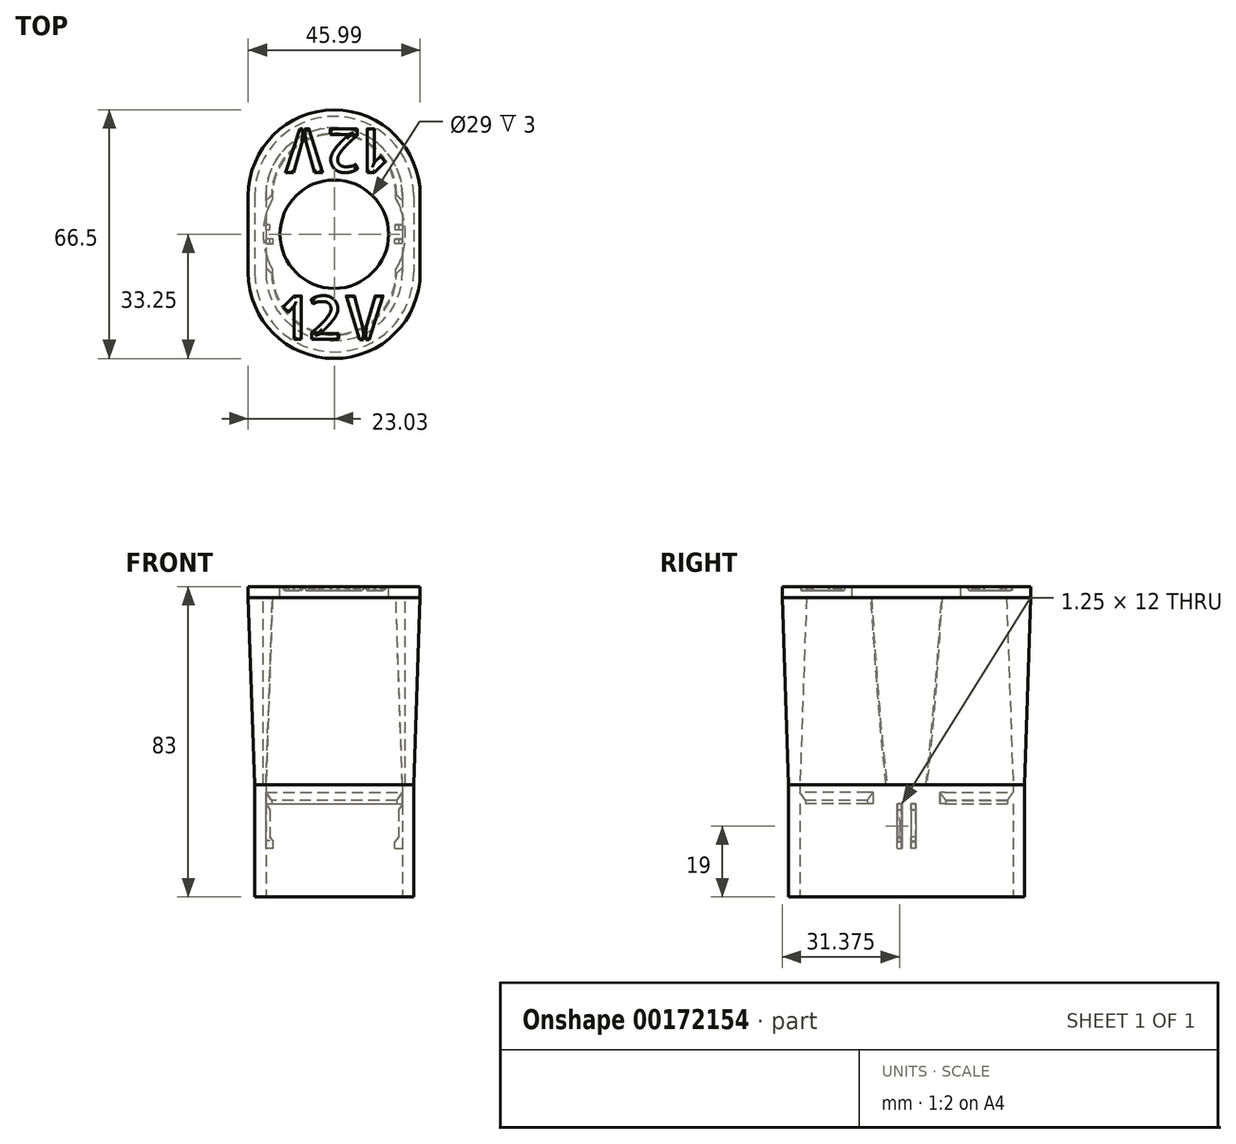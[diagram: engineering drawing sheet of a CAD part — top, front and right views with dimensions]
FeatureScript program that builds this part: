
annotation { "Feature Type Name" : "Feature", "Feature Type Description" : "" }
export const myFeature = defineFeature(function(context is Context, id is Id, definition is map)
    precondition{}
    {
        {
            var Q0;
            Q0=qCreatedBy(makeId("Top.planeOp"),FACE);
            var sketch = newSketch(context, id + "F0", { "sketchPlane" : qUnion([Q0])});
            skLineSegment(sketch, "E0", {"start": v(-18.28, 10.25) * mm, "end": v(-18.28, -10.25) * mm});
            skLineSegment(sketch, "E1", {"start": v(18.22, 10.25) * mm, "end": v(18.22, -10.25) * mm});
            skArc(sketch, "E2", {"start": v(18.22, 10.25) * mm, "mid": v(-0.03, 28.5) * mm, "end": v(-18.28, 10.25) * mm});
            skArc(sketch, "E3", {"start": v(-18.28, -10.25) * mm, "mid": v(-0.03, -28.5) * mm, "end": v(18.22, -10.25) * mm});
            skPoint(sketch, "E4", {"position": v(-0.03, 28.5) * mm});
            skPoint(sketch, "E5", {"position": v(-0.03, -28.5) * mm});
            skLineSegment(sketch, "E6.0", {"start": v(21.22, 10.25) * mm, "end": v(21.22, -10.25) * mm});
            skArc(sketch, "E6.1", {"start": v(21.22, 10.25) * mm, "mid": v(-0.03, 31.5) * mm, "end": v(-21.28, 10.25) * mm});
            skLineSegment(sketch, "E6.2", {"start": v(-21.28, 10.25) * mm, "end": v(-21.28, -10.25) * mm});
            skArc(sketch, "E6.3", {"start": v(-21.28, -10.25) * mm, "mid": v(-0.03, -31.5) * mm, "end": v(21.22, -10.25) * mm});
            skPoint(sketch, "E7", {"position": v(-18.28, 0) * mm});
            skSolve(sketch);
        }
        {
            var Q0;
            Q0=makeQuery(id+"F0.imprint","IMPRINT",FACE,{"disambiguationData":[TD([[makeQuery(id+"F0.imprint","IMPRINT",EDGE,{"derivedFrom":sQuery(id+"F0.wireOp",EDGE,"E0")}),-1.0]])]});
            extrude(context, id + "F1", {"entities" : qUnion([Q0]), "depth" : 50 * mm, "hasDraft" : true, "draftAngle" : 2 * degree, "hasSecondDirection" : true, "secondDirectionOppositeDirection" : true, "secondDirectionDepth" : 30 * mm});
        }
        {
            var Q0;
            Q0=makeQuery(id+"F1.opExtrude","CAP_FACE",FACE,{"disambiguationData":[OSD([sQuery(id+"F0.wireOp",EDGE,"E0"),sQuery(id+"F0.wireOp",EDGE,"E1"),sQuery(id+"F0.wireOp",EDGE,"E2"),sQuery(id+"F0.wireOp",EDGE,"E3"),sQuery(id+"F0.wireOp",EDGE,"E6.0"),sQuery(id+"F0.wireOp",EDGE,"E6.1"),sQuery(id+"F0.wireOp",EDGE,"E6.2"),sQuery(id+"F0.wireOp",EDGE,"E6.3")])],"isStart":false});
            var sketch = newSketch(context, id + "F2", { "sketchPlane" : qUnion([Q0])});
            skCircle(sketch, "E8", {"center": v(0, 0) * mm, "radius": 19 * mm});
            skSolve(sketch);
        }
        {
            var Q0;
            Q0 = qSketchRegion(id + "F2", true);
            extrude(context, id + "F3", {"entities" : qUnion([Q0]), "operationType" : NewBodyOperationType.REMOVE, "endBound" : BoundingType.SYMMETRIC, "oppositeDirection" : true, "depth" : 100 * mm});
        }
        {
            var Q0;
            Q0=makeQuery(id+"F1.opExtrude","CAP_FACE",FACE,{"disambiguationData":[OSD([sQuery(id+"F0.wireOp",EDGE,"E0"),sQuery(id+"F0.wireOp",EDGE,"E1"),sQuery(id+"F0.wireOp",EDGE,"E2"),sQuery(id+"F0.wireOp",EDGE,"E3"),sQuery(id+"F0.wireOp",EDGE,"E6.0"),sQuery(id+"F0.wireOp",EDGE,"E6.1"),sQuery(id+"F0.wireOp",EDGE,"E6.2"),sQuery(id+"F0.wireOp",EDGE,"E6.3")])],"isStart":false});
            var sketch = newSketch(context, id + "F4", { "sketchPlane" : qUnion([Q0])});
            skLineSegment(sketch, "E9", {"start": v(22.96, 10.25) * mm, "end": v(22.96, -10.25) * mm});
            skLineSegment(sketch, "E10", {"start": v(-23.03, 10.25) * mm, "end": v(-23.03, -10.25) * mm});
            skArc(sketch, "E11", {"start": v(22.96, 10.25) * mm, "mid": v(-0.03, 33.25) * mm, "end": v(-23.03, 10.25) * mm});
            skArc(sketch, "E12", {"start": v(-23.03, -10.25) * mm, "mid": v(-0.03, -33.25) * mm, "end": v(22.96, -10.25) * mm});
            skSolve(sketch);
        }
        {
            var Q0;
            Q0 = qSketchRegion(id + "F4", true);
            extrude(context, id + "F5", {"entities" : qUnion([Q0]), "operationType" : NewBodyOperationType.ADD, "depth" : 3 * mm});
        }
        {
            var Q0;
            Q0=makeQuery(id+"F5.opExtrude","CAP_FACE",FACE,{"disambiguationData":[OSD([sQuery(id+"F4.wireOp",EDGE,"E9"),sQuery(id+"F4.wireOp",EDGE,"E10"),sQuery(id+"F4.wireOp",EDGE,"E11"),sQuery(id+"F4.wireOp",EDGE,"E12")])],"isStart":false});
            var sketch = newSketch(context, id + "F6", { "sketchPlane" : qUnion([Q0])});
            skCircle(sketch, "E13", {"center": v(0, 0) * mm, "radius": 14.5 * mm});
            skSolve(sketch);
        }
        {
            var Q0;
            Q0 = qSketchRegion(id + "F6", true);
            extrude(context, id + "F7", {"entities" : qUnion([Q0]), "operationType" : NewBodyOperationType.REMOVE, "oppositeDirection" : true, "depth" : 25 * mm});
        }
        {
            var Q0;
            Q0=makeQuery(id+"F1.opExtrude","CAP_FACE",FACE,{"disambiguationData":[OSD([sQuery(id+"F0.wireOp",EDGE,"E0"),sQuery(id+"F0.wireOp",EDGE,"E1"),sQuery(id+"F0.wireOp",EDGE,"E2"),sQuery(id+"F0.wireOp",EDGE,"E3"),sQuery(id+"F0.wireOp",EDGE,"E6.0"),sQuery(id+"F0.wireOp",EDGE,"E6.1"),sQuery(id+"F0.wireOp",EDGE,"E6.2"),sQuery(id+"F0.wireOp",EDGE,"E6.3")])],"isStart":true});
            var sketch = newSketch(context, id + "F8", { "sketchPlane" : qUnion([Q0])});
            skLineSegment(sketch, "E14", {"start": v(-18.28, -10.25) * mm, "end": v(-18.28, -3.5) * mm});
            skLineSegment(sketch, "E15", {"start": v(18.22, -10.25) * mm, "end": v(18.22, -3.5) * mm});
            skArc(sketch, "E16", {"start": v(-18.28, -10.25) * mm, "mid": v(-0.03, -28.5) * mm, "end": v(18.22, -10.25) * mm});
            skArc(sketch, "E17", {"start": v(18.22, 10.25) * mm, "mid": v(-0.03, 28.5) * mm, "end": v(-18.28, 10.25) * mm});
            skLineSegment(sketch, "E18.0", {"start": v(-16.78, -10.25) * mm, "end": v(-16.78, -3.5) * mm});
            skArc(sketch, "E18.1", {"start": v(-16.78, -10.25) * mm, "mid": v(-0.03, -27) * mm, "end": v(16.72, -10.25) * mm});
            skLineSegment(sketch, "E18.2", {"start": v(16.72, -10.25) * mm, "end": v(16.72, -3.5) * mm});
            skArc(sketch, "E18.3", {"start": v(16.72, 10.25) * mm, "mid": v(-0.03, 27) * mm, "end": v(-16.78, 10.25) * mm});
            skPoint(sketch, "E19", {"position": v(-16.78, 0) * mm});
            skPoint(sketch, "E20", {"position": v(16.72, 0) * mm});
            skLineSegment(sketch, "E21.bottom", {"start": v(18.22, 3.5) * mm, "end": v(16.72, 3.5) * mm});
            skLineSegment(sketch, "E21.top", {"start": v(18.22, -3.5) * mm, "end": v(16.72, -3.5) * mm});
            skLineSegment(sketch, "E22.bottom", {"start": v(-18.28, 3.5) * mm, "end": v(-16.78, 3.5) * mm});
            skLineSegment(sketch, "E22.top", {"start": v(-18.28, -3.5) * mm, "end": v(-16.78, -3.5) * mm});
            skLineSegment(sketch, "E23.trimOffspring", {"start": v(-16.78, 3.5) * mm, "end": v(-16.78, 10.25) * mm});
            skPoint(sketch, "E22.right.end.orphan", {"position": v(-15.28, -3.5) * mm});
            skPoint(sketch, "E22.right.start.orphan", {"position": v(-15.28, 3.5) * mm});
            skLineSegment(sketch, "E24.trimOffspring", {"start": v(-18.28, 3.5) * mm, "end": v(-18.28, 10.25) * mm});
            skPoint(sketch, "E25.orphan", {"position": v(15.22, -3.5) * mm});
            skPoint(sketch, "E26.orphan", {"position": v(15.22, 3.5) * mm});
            skLineSegment(sketch, "E27.trimOffspring", {"start": v(16.72, 3.5) * mm, "end": v(16.72, 10.25) * mm});
            skLineSegment(sketch, "E28.trimOffspring", {"start": v(18.22, 3.5) * mm, "end": v(18.22, 10.25) * mm});
            skSolve(sketch);
        }
        {
            var Q0;
            Q0=makeQuery(id+"F8.imprint","IMPRINT",FACE,{"disambiguationData":[TD([[makeQuery(id+"F8.imprint","IMPRINT",EDGE,{"derivedFrom":sQuery(id+"F8.wireOp",EDGE,"E17")}),-1.0]])]});
            var Q1;
            Q1=makeQuery(id+"F8.imprint","IMPRINT",FACE,{"disambiguationData":[TD([[makeQuery(id+"F8.imprint","IMPRINT",EDGE,{"derivedFrom":sQuery(id+"F8.wireOp",EDGE,"E14")}),-1.0]])]});
            extrude(context, id + "F9", {"entities" : qUnion([Q0, Q1]), "operationType" : NewBodyOperationType.ADD, "oppositeDirection" : true, "depth" : 28 * mm, "hasSecondDirection" : true, "secondDirectionOppositeDirection" : true, "secondDirectionDepth" : 25 * mm});
        }
        {
            var Q0;
            Q0=makeQuery(id+"F9.opExtrude","SWEPT_EDGE",EDGE,{"disambiguationData":[OSD([sQuery(id+"F8.wireOp",EDGE,"E21.bottom"),sQuery(id+"F8.wireOp",EDGE,"E27.trimOffspring")])]});
            var Q1;
            Q1=makeQuery(id+"F9.opExtrude","SWEPT_EDGE",EDGE,{"disambiguationData":[OSD([sQuery(id+"F8.wireOp",EDGE,"E18.2"),sQuery(id+"F8.wireOp",EDGE,"E21.top")])]});
            var Q2;
            Q2=makeQuery(id+"F9.opExtrude","SWEPT_EDGE",EDGE,{"disambiguationData":[OSD([sQuery(id+"F8.wireOp",EDGE,"E22.bottom"),sQuery(id+"F8.wireOp",EDGE,"E23.trimOffspring")])]});
            var Q3;
            Q3=makeQuery(id+"F9.opExtrude","SWEPT_EDGE",EDGE,{"disambiguationData":[OSD([sQuery(id+"F8.wireOp",EDGE,"E18.0"),sQuery(id+"F8.wireOp",EDGE,"E22.top")])]});
            chamfer(context, id + "F10", {"entities" : qUnion([Q0, Q1, Q2, Q3]), "width" : 7 * mm, "tangentPropagation" : true});
        }
        {
            var Q0;
            Q0=makeQuery(id+"F9.opExtrude","CAP_EDGE",EDGE,{"disambiguationData":[OSD([sQuery(id+"F8.wireOp",EDGE,"E18.1")])],"isStart":false});
            var Q1;
            Q1=makeQuery(id+"F9.opExtrude","CAP_EDGE",EDGE,{"disambiguationData":[OSD([sQuery(id+"F8.wireOp",EDGE,"E18.3")])],"isStart":false});
            chamfer(context, id + "F11", {"entities" : qUnion([Q0, Q1]), "chamferType" : ChamferType.OFFSET_ANGLE, "width" : 1.5 * mm, "oppositeDirection" : false, "angle" : 55 * degree, "tangentPropagation" : true});
        }
        {
            var Q0;
            Q0=makeQuery(id+"F1.*.split.splitOp","SPLIT",FACE,{"derivedFrom":makeQuery(id+"F1.opExtrude","SWEPT_FACE",FACE,{"disambiguationData":[OSD([sQuery(id+"F0.wireOp",EDGE,"E1")])]}),"isFromBackBody":true});
            var sketch = newSketch(context, id + "F12", { "sketchPlane" : qUnion([Q0])});
            skLineSegment(sketch, "E29.top", {"start": v(-2.5, -5) * mm, "end": v(-1.25, -5) * mm});
            skPoint(sketch, "E30", {"position": v(0, -5) * mm});
            skLineSegment(sketch, "E31.bottom", {"start": v(2.5, -17) * mm, "end": v(1.25, -17) * mm});
            skLineSegment(sketch, "E31.left", {"start": v(2.5, -17) * mm, "end": v(2.5, -15) * mm});
            skLineSegment(sketch, "E31.right", {"start": v(-2.5, -17) * mm, "end": v(-2.5, -15) * mm});
            skLineSegment(sketch, "E32.bottom", {"start": v(-2.5, -17) * mm, "end": v(-1.25, -17) * mm});
            skLineSegment(sketch, "E32.top", {"start": v(-2.5, -15) * mm, "end": v(-1.25, -15) * mm});
            skLineSegment(sketch, "E33.left", {"start": v(1.25, -17) * mm, "end": v(1.25, -15) * mm});
            skLineSegment(sketch, "E33.right", {"start": v(-1.25, -17) * mm, "end": v(-1.25, -15) * mm});
            skLineSegment(sketch, "E34.trimOffspring", {"start": v(1.25, -15) * mm, "end": v(2.5, -15) * mm});
            skLineSegment(sketch, "E35.trimOffspring", {"start": v(1.25, -17) * mm, "end": v(2.5, -17) * mm});
            skLineSegment(sketch, "E36.trimOffspring", {"start": v(-1.25, -17) * mm, "end": v(-2.5, -17) * mm});
            skLineSegment(sketch, "E37.trimOffspring", {"start": v(1.25, -5) * mm, "end": v(2.5, -5) * mm});
            skLineSegment(sketch, "E38", {"start": v(-2.5, -5) * mm, "end": v(-2.5, -15) * mm});
            skLineSegment(sketch, "E39", {"start": v(-1.25, -5) * mm, "end": v(-1.25, -15) * mm});
            skLineSegment(sketch, "E40", {"start": v(1.25, -5) * mm, "end": v(1.25, -15) * mm});
            skLineSegment(sketch, "E41", {"start": v(2.5, -15) * mm, "end": v(2.5, -5) * mm});
            skSolve(sketch);
        }
        {
            var Q0;
            Q0=makeQuery(id+"F12.imprint","IMPRINT",FACE,{"disambiguationData":[TD([[makeQuery(id+"F12.imprint","IMPRINT",EDGE,{"derivedFrom":sQuery(id+"F12.wireOp",EDGE,"E34.trimOffspring")}),1.0]])]});
            var Q1;
            Q1=makeQuery(id+"F12.imprint","IMPRINT",FACE,{"disambiguationData":[TD([[makeQuery(id+"F12.imprint","IMPRINT",EDGE,{"derivedFrom":sQuery(id+"F12.wireOp",EDGE,"E29.top")}),-1.0]])]});
            extrude(context, id + "F13", {"entities" : qUnion([Q0, Q1]), "operationType" : NewBodyOperationType.ADD, "depth" : 1 * mm});
        }
        {
            var Q0;
            Q0=makeQuery(id+"F12.imprint","IMPRINT",FACE,{"disambiguationData":[TD([[makeQuery(id+"F12.imprint","IMPRINT",EDGE,{"derivedFrom":sQuery(id+"F12.wireOp",EDGE,"E31.left")}),1.0]])]});
            var Q1;
            Q1=makeQuery(id+"F12.imprint","IMPRINT",FACE,{"disambiguationData":[TD([[makeQuery(id+"F12.imprint","IMPRINT",EDGE,{"derivedFrom":sQuery(id+"F12.wireOp",EDGE,"E32.top")}),-1.0]])]});
            extrude(context, id + "F14", {"entities" : qUnion([Q0, Q1]), "operationType" : NewBodyOperationType.ADD, "depth" : 2 * mm});
        }
        {
            var Q0;
            Q0=makeQuery(id+"F1.*.split.splitOp","SPLIT",FACE,{"derivedFrom":makeQuery(id+"F1.opExtrude","SWEPT_FACE",FACE,{"disambiguationData":[OSD([sQuery(id+"F0.wireOp",EDGE,"E0")])]}),"isFromBackBody":true});
            var sketch = newSketch(context, id + "F15", { "sketchPlane" : qUnion([Q0])});
            skLineSegment(sketch, "E42.top", {"start": v(-2.52, -5) * mm, "end": v(-1.27, -5) * mm});
            skLineSegment(sketch, "E43.bottom", {"start": v(2.48, -17) * mm, "end": v(1.23, -17) * mm});
            skLineSegment(sketch, "E43.left", {"start": v(2.48, -17) * mm, "end": v(2.48, -15) * mm});
            skLineSegment(sketch, "E43.right", {"start": v(-2.52, -17) * mm, "end": v(-2.52, -15) * mm});
            skLineSegment(sketch, "E44.bottom", {"start": v(-2.52, -17) * mm, "end": v(-1.27, -17) * mm});
            skLineSegment(sketch, "E44.top", {"start": v(-2.52, -15) * mm, "end": v(-1.27, -15) * mm});
            skLineSegment(sketch, "E45.left", {"start": v(1.23, -17) * mm, "end": v(1.23, -15) * mm});
            skLineSegment(sketch, "E45.right", {"start": v(-1.27, -17) * mm, "end": v(-1.27, -15) * mm});
            skLineSegment(sketch, "E46.trimOffspring", {"start": v(1.23, -15) * mm, "end": v(2.48, -15) * mm});
            skLineSegment(sketch, "E47.trimOffspring", {"start": v(1.23, -17) * mm, "end": v(2.48, -17) * mm});
            skLineSegment(sketch, "E48.trimOffspring", {"start": v(-1.27, -17) * mm, "end": v(-2.52, -17) * mm});
            skLineSegment(sketch, "E49.trimOffspring", {"start": v(1.23, -5) * mm, "end": v(2.48, -5) * mm});
            skLineSegment(sketch, "E50", {"start": v(-2.52, -5) * mm, "end": v(-2.52, -15) * mm});
            skLineSegment(sketch, "E51", {"start": v(-1.27, -5) * mm, "end": v(-1.27, -15) * mm});
            skLineSegment(sketch, "E52", {"start": v(1.23, -5) * mm, "end": v(1.23, -15) * mm});
            skLineSegment(sketch, "E53", {"start": v(2.48, -15) * mm, "end": v(2.48, -5) * mm});
            skSolve(sketch);
        }
        {
            var Q0;
            Q0=makeQuery(id+"F15.imprint","IMPRINT",FACE,{"disambiguationData":[TD([[makeQuery(id+"F15.imprint","IMPRINT",EDGE,{"derivedFrom":sQuery(id+"F15.wireOp",EDGE,"E44.top")}),-1.0]])]});
            var Q1;
            Q1=makeQuery(id+"F15.imprint","IMPRINT",FACE,{"disambiguationData":[TD([[makeQuery(id+"F15.imprint","IMPRINT",EDGE,{"derivedFrom":sQuery(id+"F15.wireOp",EDGE,"E43.left")}),1.0]])]});
            extrude(context, id + "F16", {"entities" : qUnion([Q0, Q1]), "operationType" : NewBodyOperationType.ADD, "depth" : 2 * mm});
        }
        {
            var Q0;
            Q0=makeQuery(id+"F15.imprint","IMPRINT",FACE,{"disambiguationData":[TD([[makeQuery(id+"F15.imprint","IMPRINT",EDGE,{"derivedFrom":sQuery(id+"F15.wireOp",EDGE,"E46.trimOffspring")}),1.0]])]});
            var Q1;
            Q1=makeQuery(id+"F15.imprint","IMPRINT",FACE,{"disambiguationData":[TD([[makeQuery(id+"F15.imprint","IMPRINT",EDGE,{"derivedFrom":sQuery(id+"F15.wireOp",EDGE,"E42.top")}),-1.0]])]});
            extrude(context, id + "F17", {"entities" : qUnion([Q0, Q1]), "operationType" : NewBodyOperationType.ADD, "depth" : 1 * mm});
        }
        {
            var Q0;
            Q0=makeQuery(id+"F17.opExtrude","CAP_EDGE",EDGE,{"disambiguationData":[OSD([sQuery(id+"F15.wireOp",EDGE,"E49.trimOffspring")])],"isStart":false});
            var Q1;
            Q1=makeQuery(id+"F17.opExtrude","CAP_EDGE",EDGE,{"disambiguationData":[OSD([sQuery(id+"F15.wireOp",EDGE,"E42.top")])],"isStart":false});
            var Q2;
            Q2=makeQuery(id+"F13.opExtrude","CAP_EDGE",EDGE,{"disambiguationData":[OSD([sQuery(id+"F12.wireOp",EDGE,"E29.top")])],"isStart":false});
            var Q3;
            Q3=makeQuery(id+"F13.opExtrude","CAP_EDGE",EDGE,{"disambiguationData":[OSD([sQuery(id+"F12.wireOp",EDGE,"E37.trimOffspring")])],"isStart":false});
            chamfer(context, id + "F18", {"entities" : qUnion([Q0, Q1, Q2, Q3]), "chamferType" : ChamferType.OFFSET_ANGLE, "width" : 1 * mm, "oppositeDirection" : false, "angle" : 60 * degree, "tangentPropagation" : true});
        }
        {
            var Q0;
            Q0=makeQuery(id+"F14.opExtrude","SWEPT_FACE",FACE,{"disambiguationData":[OSD([sQuery(id+"F12.wireOp",EDGE,"E34.trimOffspring")])]});
            var Q1;
            Q1=makeQuery(id+"F14.opExtrude","SWEPT_FACE",FACE,{"disambiguationData":[OSD([sQuery(id+"F12.wireOp",EDGE,"E32.top")])]});
            var Q2;
            Q2=makeQuery(id+"F16.opExtrude","SWEPT_FACE",FACE,{"disambiguationData":[OSD([sQuery(id+"F15.wireOp",EDGE,"E46.trimOffspring")])]});
            var Q3;
            Q3=makeQuery(id+"F16.opExtrude","SWEPT_FACE",FACE,{"disambiguationData":[OSD([sQuery(id+"F15.wireOp",EDGE,"E44.top")])]});
            extrude(context, id + "F19", {"entities" : qUnion([Q0, Q1, Q2, Q3]), "operationType" : NewBodyOperationType.ADD, "depth" : 1 * mm});
        }
        {
            var Q0;
            {var subQ0=sQuery(id+"F12.wireOp",EDGE,"E34.trimOffspring");Q0=makeQuery(id+"F19.opExtrude","CAP_EDGE",EDGE,{"disambiguationData":[OSD([subQ0]),TDD([makeQuery(id+"F14.opExtrude","CAP_EDGE",EDGE,{"disambiguationData":[OSD([subQ0])],"isStart":false})])],"isStart":false});}
            var Q1;
            {var subQ0=sQuery(id+"F12.wireOp",EDGE,"E32.top");Q1=makeQuery(id+"F19.opExtrude","CAP_EDGE",EDGE,{"disambiguationData":[OSD([subQ0]),TDD([makeQuery(id+"F14.opExtrude","CAP_EDGE",EDGE,{"disambiguationData":[OSD([subQ0])],"isStart":false})])],"isStart":false});}
            var Q2;
            {var subQ0=sQuery(id+"F15.wireOp",EDGE,"E46.trimOffspring");Q2=makeQuery(id+"F19.opExtrude","CAP_EDGE",EDGE,{"disambiguationData":[OSD([subQ0]),TDD([makeQuery(id+"F16.opExtrude","CAP_EDGE",EDGE,{"disambiguationData":[OSD([subQ0])],"isStart":false})])],"isStart":false});}
            var Q3;
            {var subQ0=sQuery(id+"F15.wireOp",EDGE,"E44.top");Q3=makeQuery(id+"F19.opExtrude","CAP_EDGE",EDGE,{"disambiguationData":[OSD([subQ0]),TDD([makeQuery(id+"F16.opExtrude","CAP_EDGE",EDGE,{"disambiguationData":[OSD([subQ0])],"isStart":false})])],"isStart":false});}
            chamfer(context, id + "F20", {"entities" : qUnion([Q0, Q1, Q2, Q3]), "chamferType" : ChamferType.OFFSET_ANGLE, "width" : 1 * mm, "oppositeDirection" : false, "angle" : 50 * degree, "tangentPropagation" : true});
        }
        {
            var Q0;
            Q0=makeQuery(id+"F5.opExtrude","CAP_FACE",FACE,{"disambiguationData":[OSD([sQuery(id+"F4.wireOp",EDGE,"E9"),sQuery(id+"F4.wireOp",EDGE,"E10"),sQuery(id+"F4.wireOp",EDGE,"E11"),sQuery(id+"F4.wireOp",EDGE,"E12")])],"isStart":false});
            var sketch = newSketch(context, id + "F21", { "sketchPlane" : qUnion([Q0])});
            skText(sketch, "E54", { "text": "12V", "fontName": "AllertaStencil-Regular.ttf"});
            skText(sketch, "E55", { "text": "12V", "fontName": "AllertaStencil-Regular.ttf"});
            skLineSegment(sketch, "E56", {"start": v(0, -16.5) * mm, "end": v(0, 0) * mm});
            skLineSegment(sketch, "E57", {"start": v(0, 0) * mm, "end": v(0, 16.5) * mm});
            const initialGuessF21  = {"E54": [-0.01414, -0.02815, 1, 0, 0.01165], "E55": [0.01414, 0.02815, -1, 0, 0.01165]};
            skSetInitialGuess(sketch, initialGuessF21);
            skSolve(sketch);
        }
        {
            var Q0;
            Q0=makeQuery(id+"F21.imprint","IMPRINT",FACE,{"disambiguationData":[TD([[makeQuery(id+"F21.imprint","IMPRINT",EDGE,{"derivedFrom":sQuery(id+"F21.wireOp",EDGE,"E54.sketch_text.stroke-45")}),-1.0]])]});
            var Q1;
            Q1=makeQuery(id+"F21.imprint","IMPRINT",FACE,{"disambiguationData":[TD([[makeQuery(id+"F21.imprint","IMPRINT",EDGE,{"derivedFrom":sQuery(id+"F21.wireOp",EDGE,"E54.sketch_text.stroke-40")}),-1.0]])]});
            var Q2;
            Q2=makeQuery(id+"F21.imprint","IMPRINT",FACE,{"disambiguationData":[TD([[makeQuery(id+"F21.imprint","IMPRINT",EDGE,{"derivedFrom":sQuery(id+"F21.wireOp",EDGE,"E54.sketch_text.stroke-7")}),-1.0]])]});
            var Q3;
            Q3=makeQuery(id+"F21.imprint","IMPRINT",FACE,{"disambiguationData":[TD([[makeQuery(id+"F21.imprint","IMPRINT",EDGE,{"derivedFrom":sQuery(id+"F21.wireOp",EDGE,"E54.sketch_text.stroke-0")}),-1.0]])]});
            var Q4;
            Q4=makeQuery(id+"F21.imprint","IMPRINT",FACE,{"disambiguationData":[TD([[makeQuery(id+"F21.imprint","IMPRINT",EDGE,{"derivedFrom":sQuery(id+"F21.wireOp",EDGE,"E55.sketch_text.stroke-0")}),-1.0]])]});
            var Q5;
            Q5=makeQuery(id+"F21.imprint","IMPRINT",FACE,{"disambiguationData":[TD([[makeQuery(id+"F21.imprint","IMPRINT",EDGE,{"derivedFrom":sQuery(id+"F21.wireOp",EDGE,"E55.sketch_text.stroke-7")}),-1.0]])]});
            var Q6;
            Q6=makeQuery(id+"F21.imprint","IMPRINT",FACE,{"disambiguationData":[TD([[makeQuery(id+"F21.imprint","IMPRINT",EDGE,{"derivedFrom":sQuery(id+"F21.wireOp",EDGE,"E55.sketch_text.stroke-40")}),-1.0]])]});
            var Q7;
            Q7=makeQuery(id+"F21.imprint","IMPRINT",FACE,{"disambiguationData":[TD([[makeQuery(id+"F21.imprint","IMPRINT",EDGE,{"derivedFrom":sQuery(id+"F21.wireOp",EDGE,"E55.sketch_text.stroke-45")}),-1.0]])]});
            extrude(context, id + "F22", {"entities" : qUnion([Q0, Q1, Q2, Q3, Q4, Q5, Q6, Q7]), "operationType" : NewBodyOperationType.REMOVE, "oppositeDirection" : true, "depth" : 1 * mm});
        }
        {
            var Q0;
            Q0=makeQuery(id+"F22.boolean.opBoolean","COPY",FACE,{"derivedFrom":makeQuery(id+"F22.opExtrude","CAP_FACE",FACE,{"disambiguationData":[OSD([sQuery(id+"F21.wireOp",EDGE,"E54.sketch_text.stroke-0"),sQuery(id+"F21.wireOp",EDGE,"E54.sketch_text.stroke-1"),sQuery(id+"F21.wireOp",EDGE,"E54.sketch_text.stroke-2"),sQuery(id+"F21.wireOp",EDGE,"E54.sketch_text.stroke-3"),sQuery(id+"F21.wireOp",EDGE,"E54.sketch_text.stroke-4"),sQuery(id+"F21.wireOp",EDGE,"E54.sketch_text.stroke-5"),sQuery(id+"F21.wireOp",EDGE,"E54.sketch_text.stroke-6")])],"isStart":false})});
            var Q1;
            Q1=makeQuery(id+"F22.boolean.opBoolean","COPY",FACE,{"derivedFrom":makeQuery(id+"F22.opExtrude","CAP_FACE",FACE,{"disambiguationData":[OSD([sQuery(id+"F21.wireOp",EDGE,"E54.sketch_text.stroke-7"),sQuery(id+"F21.wireOp",EDGE,"E54.sketch_text.stroke-8"),sQuery(id+"F21.wireOp",EDGE,"E54.sketch_text.stroke-9"),sQuery(id+"F21.wireOp",EDGE,"E54.sketch_text.stroke-10"),sQuery(id+"F21.wireOp",EDGE,"E54.sketch_text.stroke-11"),sQuery(id+"F21.wireOp",EDGE,"E54.sketch_text.stroke-12"),sQuery(id+"F21.wireOp",EDGE,"E54.sketch_text.stroke-13"),sQuery(id+"F21.wireOp",EDGE,"E54.sketch_text.stroke-14"),sQuery(id+"F21.wireOp",EDGE,"E54.sketch_text.stroke-15"),sQuery(id+"F21.wireOp",EDGE,"E54.sketch_text.stroke-16"),sQuery(id+"F21.wireOp",EDGE,"E54.sketch_text.stroke-17"),sQuery(id+"F21.wireOp",EDGE,"E54.sketch_text.stroke-18"),sQuery(id+"F21.wireOp",EDGE,"E54.sketch_text.stroke-19"),sQuery(id+"F21.wireOp",EDGE,"E54.sketch_text.stroke-20"),sQuery(id+"F21.wireOp",EDGE,"E54.sketch_text.stroke-21"),sQuery(id+"F21.wireOp",EDGE,"E54.sketch_text.stroke-22"),sQuery(id+"F21.wireOp",EDGE,"E54.sketch_text.stroke-23"),sQuery(id+"F21.wireOp",EDGE,"E54.sketch_text.stroke-24"),sQuery(id+"F21.wireOp",EDGE,"E54.sketch_text.stroke-25"),sQuery(id+"F21.wireOp",EDGE,"E54.sketch_text.stroke-26"),sQuery(id+"F21.wireOp",EDGE,"E54.sketch_text.stroke-27"),sQuery(id+"F21.wireOp",EDGE,"E54.sketch_text.stroke-28"),sQuery(id+"F21.wireOp",EDGE,"E54.sketch_text.stroke-29"),sQuery(id+"F21.wireOp",EDGE,"E54.sketch_text.stroke-30"),sQuery(id+"F21.wireOp",EDGE,"E54.sketch_text.stroke-31"),sQuery(id+"F21.wireOp",EDGE,"E54.sketch_text.stroke-32"),sQuery(id+"F21.wireOp",EDGE,"E54.sketch_text.stroke-33"),sQuery(id+"F21.wireOp",EDGE,"E54.sketch_text.stroke-34"),sQuery(id+"F21.wireOp",EDGE,"E54.sketch_text.stroke-35"),sQuery(id+"F21.wireOp",EDGE,"E54.sketch_text.stroke-36"),sQuery(id+"F21.wireOp",EDGE,"E54.sketch_text.stroke-37"),sQuery(id+"F21.wireOp",EDGE,"E54.sketch_text.stroke-38"),sQuery(id+"F21.wireOp",EDGE,"E54.sketch_text.stroke-39")])],"isStart":false})});
            var Q2;
            Q2=makeQuery(id+"F22.boolean.opBoolean","COPY",FACE,{"derivedFrom":makeQuery(id+"F22.opExtrude","CAP_FACE",FACE,{"disambiguationData":[OSD([sQuery(id+"F21.wireOp",EDGE,"E54.sketch_text.stroke-40"),sQuery(id+"F21.wireOp",EDGE,"E54.sketch_text.stroke-41"),sQuery(id+"F21.wireOp",EDGE,"E54.sketch_text.stroke-42"),sQuery(id+"F21.wireOp",EDGE,"E54.sketch_text.stroke-43"),sQuery(id+"F21.wireOp",EDGE,"E54.sketch_text.stroke-44")])],"isStart":false})});
            var Q3;
            Q3=makeQuery(id+"F22.boolean.opBoolean","COPY",FACE,{"derivedFrom":makeQuery(id+"F22.opExtrude","CAP_FACE",FACE,{"disambiguationData":[OSD([sQuery(id+"F21.wireOp",EDGE,"E54.sketch_text.stroke-45"),sQuery(id+"F21.wireOp",EDGE,"E54.sketch_text.stroke-46"),sQuery(id+"F21.wireOp",EDGE,"E54.sketch_text.stroke-47"),sQuery(id+"F21.wireOp",EDGE,"E54.sketch_text.stroke-48"),sQuery(id+"F21.wireOp",EDGE,"E54.sketch_text.stroke-49")])],"isStart":false})});
            var Q4;
            Q4=makeQuery(id+"F22.boolean.opBoolean","COPY",FACE,{"derivedFrom":makeQuery(id+"F22.opExtrude","CAP_FACE",FACE,{"disambiguationData":[OSD([sQuery(id+"F21.wireOp",EDGE,"E55.sketch_text.stroke-7"),sQuery(id+"F21.wireOp",EDGE,"E55.sketch_text.stroke-8"),sQuery(id+"F21.wireOp",EDGE,"E55.sketch_text.stroke-9"),sQuery(id+"F21.wireOp",EDGE,"E55.sketch_text.stroke-10"),sQuery(id+"F21.wireOp",EDGE,"E55.sketch_text.stroke-11"),sQuery(id+"F21.wireOp",EDGE,"E55.sketch_text.stroke-12"),sQuery(id+"F21.wireOp",EDGE,"E55.sketch_text.stroke-13"),sQuery(id+"F21.wireOp",EDGE,"E55.sketch_text.stroke-14"),sQuery(id+"F21.wireOp",EDGE,"E55.sketch_text.stroke-15"),sQuery(id+"F21.wireOp",EDGE,"E55.sketch_text.stroke-16"),sQuery(id+"F21.wireOp",EDGE,"E55.sketch_text.stroke-17"),sQuery(id+"F21.wireOp",EDGE,"E55.sketch_text.stroke-18"),sQuery(id+"F21.wireOp",EDGE,"E55.sketch_text.stroke-19"),sQuery(id+"F21.wireOp",EDGE,"E55.sketch_text.stroke-20"),sQuery(id+"F21.wireOp",EDGE,"E55.sketch_text.stroke-21"),sQuery(id+"F21.wireOp",EDGE,"E55.sketch_text.stroke-22"),sQuery(id+"F21.wireOp",EDGE,"E55.sketch_text.stroke-23"),sQuery(id+"F21.wireOp",EDGE,"E55.sketch_text.stroke-24"),sQuery(id+"F21.wireOp",EDGE,"E55.sketch_text.stroke-25"),sQuery(id+"F21.wireOp",EDGE,"E55.sketch_text.stroke-26"),sQuery(id+"F21.wireOp",EDGE,"E55.sketch_text.stroke-27"),sQuery(id+"F21.wireOp",EDGE,"E55.sketch_text.stroke-28"),sQuery(id+"F21.wireOp",EDGE,"E55.sketch_text.stroke-29"),sQuery(id+"F21.wireOp",EDGE,"E55.sketch_text.stroke-30"),sQuery(id+"F21.wireOp",EDGE,"E55.sketch_text.stroke-31"),sQuery(id+"F21.wireOp",EDGE,"E55.sketch_text.stroke-32"),sQuery(id+"F21.wireOp",EDGE,"E55.sketch_text.stroke-33"),sQuery(id+"F21.wireOp",EDGE,"E55.sketch_text.stroke-34"),sQuery(id+"F21.wireOp",EDGE,"E55.sketch_text.stroke-35"),sQuery(id+"F21.wireOp",EDGE,"E55.sketch_text.stroke-36"),sQuery(id+"F21.wireOp",EDGE,"E55.sketch_text.stroke-37"),sQuery(id+"F21.wireOp",EDGE,"E55.sketch_text.stroke-38"),sQuery(id+"F21.wireOp",EDGE,"E55.sketch_text.stroke-39")])],"isStart":false})});
            var Q5;
            Q5=makeQuery(id+"F22.boolean.opBoolean","COPY",FACE,{"derivedFrom":makeQuery(id+"F22.opExtrude","CAP_FACE",FACE,{"disambiguationData":[OSD([sQuery(id+"F21.wireOp",EDGE,"E55.sketch_text.stroke-0"),sQuery(id+"F21.wireOp",EDGE,"E55.sketch_text.stroke-1"),sQuery(id+"F21.wireOp",EDGE,"E55.sketch_text.stroke-2"),sQuery(id+"F21.wireOp",EDGE,"E55.sketch_text.stroke-3"),sQuery(id+"F21.wireOp",EDGE,"E55.sketch_text.stroke-4"),sQuery(id+"F21.wireOp",EDGE,"E55.sketch_text.stroke-5"),sQuery(id+"F21.wireOp",EDGE,"E55.sketch_text.stroke-6")])],"isStart":false})});
            var Q6;
            Q6=makeQuery(id+"F22.boolean.opBoolean","COPY",FACE,{"derivedFrom":makeQuery(id+"F22.opExtrude","CAP_FACE",FACE,{"disambiguationData":[OSD([sQuery(id+"F21.wireOp",EDGE,"E55.sketch_text.stroke-40"),sQuery(id+"F21.wireOp",EDGE,"E55.sketch_text.stroke-41"),sQuery(id+"F21.wireOp",EDGE,"E55.sketch_text.stroke-42"),sQuery(id+"F21.wireOp",EDGE,"E55.sketch_text.stroke-43"),sQuery(id+"F21.wireOp",EDGE,"E55.sketch_text.stroke-44")])],"isStart":false})});
            var Q7;
            Q7=makeQuery(id+"F22.boolean.opBoolean","COPY",FACE,{"derivedFrom":makeQuery(id+"F22.opExtrude","CAP_FACE",FACE,{"disambiguationData":[OSD([sQuery(id+"F21.wireOp",EDGE,"E55.sketch_text.stroke-45"),sQuery(id+"F21.wireOp",EDGE,"E55.sketch_text.stroke-46"),sQuery(id+"F21.wireOp",EDGE,"E55.sketch_text.stroke-47"),sQuery(id+"F21.wireOp",EDGE,"E55.sketch_text.stroke-48"),sQuery(id+"F21.wireOp",EDGE,"E55.sketch_text.stroke-49")])],"isStart":false})});
            fillet(context, id + "F23", {"entities" : qUnion([Q0, Q1, Q2, Q3, Q4, Q5, Q6, Q7]), "radius" : .5 * mm, "tangentPropagation" : true, "allowEdgeOverflow" : false});
        }
    });
